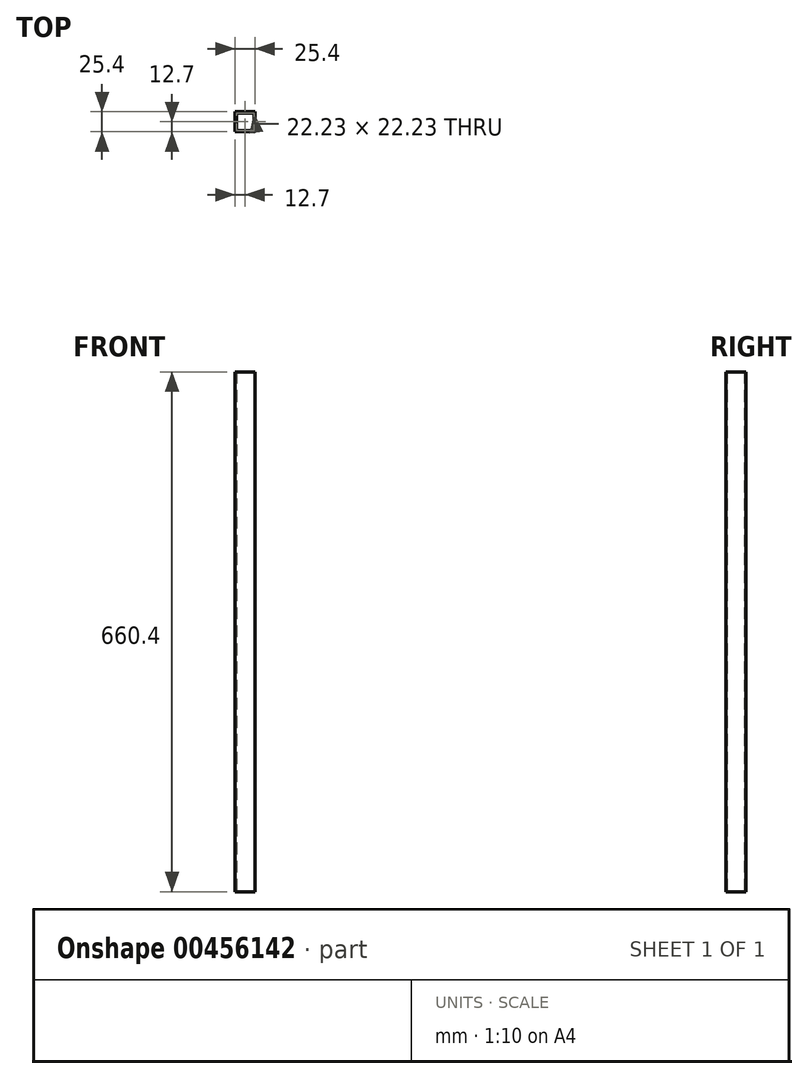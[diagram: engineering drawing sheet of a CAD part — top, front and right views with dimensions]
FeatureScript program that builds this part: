
annotation { "Feature Type Name" : "Feature", "Feature Type Description" : "" }
export const myFeature = defineFeature(function(context is Context, id is Id, definition is map)
    precondition{}
    {
        {
            var Q0;
            Q0=qCreatedBy(makeId("Right.planeOp"),FACE);
            var sketch = newSketch(context, id + "F0", { "sketchPlane" : qUnion([Q0])});
            skLineSegment(sketch, "E0.bottom", {"start": v(-12.7, 330.2) * mm, "end": v(12.7, 330.2) * mm});
            skLineSegment(sketch, "E0.top", {"start": v(-12.7, -330.2) * mm, "end": v(12.7, -330.2) * mm});
            skLineSegment(sketch, "E0.left", {"start": v(-12.7, 330.2) * mm, "end": v(-12.7, -330.2) * mm});
            skLineSegment(sketch, "E0.right", {"start": v(12.7, 330.2) * mm, "end": v(12.7, -330.2) * mm});
            skPoint(sketch, "E0.middle", {"position": v(0, 0) * mm});
            skSolve(sketch);
        }
        {
            var Q0;
            Q0=makeQuery(id+"F0.imprint","IMPRINT",FACE,{"disambiguationData":[TD([[makeQuery(id+"F0.imprint","IMPRINT",EDGE,{"derivedFrom":sQuery(id+"F0.wireOp",EDGE,"E0.bottom")}),-1.0]])]});
            extrude(context, id + "F1", {"entities" : qUnion([Q0]), "endBound" : BoundingType.SYMMETRIC, "depth" : 25.4 * mm});
        }
        {
            var Q0;
            Q0=makeQuery(id+"F1.opExtrude","SWEPT_FACE",FACE,{"disambiguationData":[OSD([sQuery(id+"F0.wireOp",EDGE,"E0.bottom")])]});
            var Q1;
            Q1=makeQuery(id+"F1.opExtrude","SWEPT_FACE",FACE,{"disambiguationData":[OSD([sQuery(id+"F0.wireOp",EDGE,"E0.top")])]});
            shell(context, id + "F2", {"entities" : qUnion([Q0, Q1]), "thickness" : 1.59 * mm});
        }
    });
